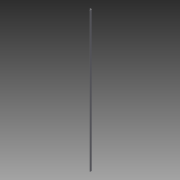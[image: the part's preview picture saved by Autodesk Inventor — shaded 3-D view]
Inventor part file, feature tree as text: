
AUTODESK INVENTOR PART (.ipt)
format: ipt  version: 2013 (Build 170138000, 138)  size: 83,456 bytes
history: native  units: in
note: dims shown in document units (in); Inventor stores cm internally (conversion verified against a paired STEP export)
features: other x2, extrude x1, sketch x1
ambient origin geometry x8: Origin, YZ Plane, XZ Plane, XY Plane, X Axis, Y Axis, Z Axis, Center Point
bodies: Solid1 (feature_tree)
feature tree (4):
  other  "Table"
  other  "Angle Iron-01"
  extrude  "Angle Iron Template"  Depth=1.0in
  sketch  "Sketch1"  dims[d2=0.1875in d3=1.0in d4=1.0in d5=0.1in d7=0.0in]
